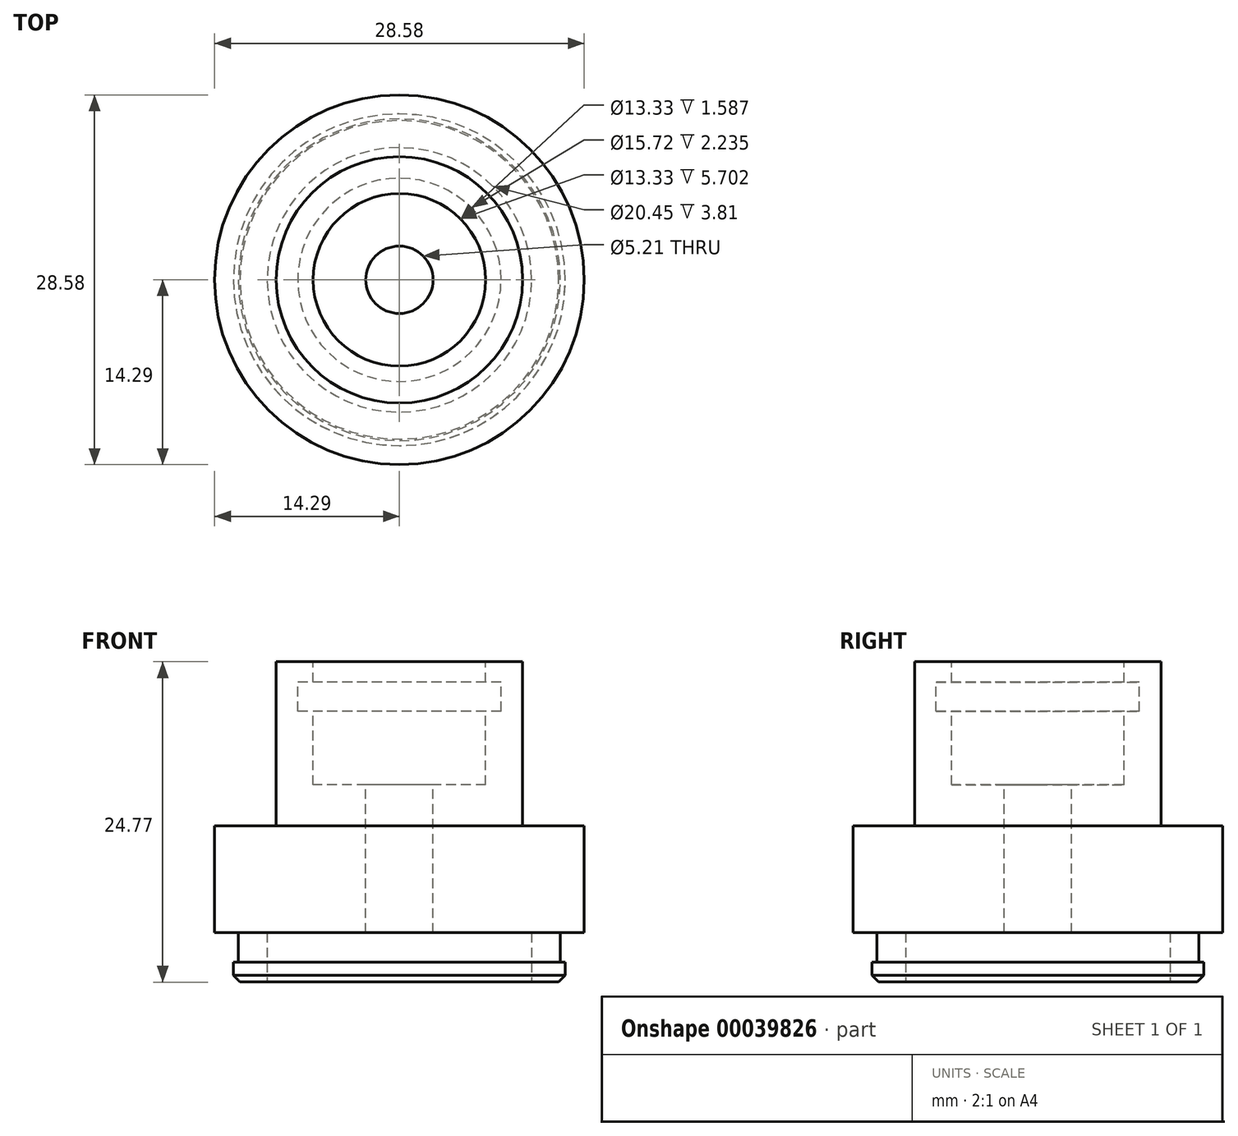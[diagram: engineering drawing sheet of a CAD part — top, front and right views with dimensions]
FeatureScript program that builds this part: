
annotation { "Feature Type Name" : "Feature", "Feature Type Description" : "" }
export const myFeature = defineFeature(function(context is Context, id is Id, definition is map)
    precondition{}
    {
        {
            var Q0;
            Q0=qCreatedBy(makeId("Top.planeOp"),FACE);
            var sketch = newSketch(context, id + "F0", { "sketchPlane" : qUnion([Q0])});
            skCircle(sketch, "E0", {"center": v(0, 0) * mm, "radius": 9.53 * mm});
            skSolve(sketch);
        }
        {
            var Q0;
            Q0=qSketchRegion(id+"F0",true);
            extrude(context, id + "F1", {"entities" : qUnion([Q0]), "depth" : 12.7 * mm});
        }
        {
            var Q0;
            Q0=makeQuery(id+"F1.opExtrude","CAP_FACE",FACE,{"disambiguationData":[OSD([sQuery(id+"F0.wireOp",EDGE,"E0")])],"isStart":false});
            var sketch = newSketch(context, id + "F2", { "sketchPlane" : qUnion([Q0])});
            skCircle(sketch, "E1", {"center": v(0, 0) * mm, "radius": 6.67 * mm});
            skSolve(sketch);
        }
        {
            var Q0;
            Q0=qSketchRegion(id+"F2",true);
            extrude(context, id + "F3", {"entities" : qUnion([Q0]), "operationType" : NewBodyOperationType.REMOVE, "oppositeDirection" : true, "depth" : 9.52 * mm});
        }
        {
            var Q0;
            Q0=qCreatedBy(makeId("Front.planeOp"),FACE);
            var sketch = newSketch(context, id + "F4", { "sketchPlane" : qUnion([Q0])});
            skLineSegment(sketch, "E2.bottom", {"start": v(6.67, 11.11) * mm, "end": v(7.86, 11.11) * mm});
            skLineSegment(sketch, "E2.top", {"start": v(6.67, 8.88) * mm, "end": v(7.86, 8.88) * mm});
            skLineSegment(sketch, "E2.left", {"start": v(6.67, 11.11) * mm, "end": v(6.67, 8.88) * mm});
            skLineSegment(sketch, "E2.right", {"start": v(7.86, 11.11) * mm, "end": v(7.86, 8.88) * mm});
            skLineSegment(sketch, "E3", {"start": v(0, 0) * mm, "end": v(0, 38.04) * mm, "construction": true});
            skSolve(sketch);
        }
        {
            var Q0;
            Q0=qSketchRegion(id+"F4",true);
            var Q1;
            Q1=sQuery(id+"F4.wireOp",EDGE,"E3");
            revolve(context, id + "F5", {"operationType" : NewBodyOperationType.REMOVE, "entities" : qUnion([Q0]), "axis" : qUnion([Q1]), "revolveType" : RevolveType.FULL, "oppositeDirection" : true});
        }
        {
            var Q0;
            Q0=makeQuery(id+"F1.opExtrude","CAP_FACE",FACE,{"disambiguationData":[OSD([sQuery(id+"F0.wireOp",EDGE,"E0")])],"isStart":true});
            var sketch = newSketch(context, id + "F6", { "sketchPlane" : qUnion([Q0])});
            skCircle(sketch, "E4", {"center": v(0, 0) * mm, "radius": 14.29 * mm});
            skSolve(sketch);
        }
        {
            var Q0;
            Q0=makeQuery(id+"F6.imprint","IMPRINT",FACE,{"disambiguationData":[TD([[makeQuery(id+"F6.imprint","IMPRINT",EDGE,{"derivedFrom":sQuery(id+"F6.wireOp",EDGE,"E4")}),1.0]])]});
            var Q1;
            Q1=makeQuery(id+"F6.imprint","IMPRINT",FACE,{"disambiguationData":[TD([[makeQuery(id+"F6.imprint","IMPRINT",EDGE,{"derivedFrom":makeQuery(id+"F15.boolean.opBoolean","INTERSECT",EDGE,{"derivedFrom":[makeQuery(id+"F1.opExtrude","CAP_FACE",FACE,{"disambiguationData":[OSD([sQuery(id+"F0.wireOp",EDGE,"E0")])],"isStart":true}),makeQuery(id+"F15.opExtrude","SWEPT_FACE",FACE,{"disambiguationData":[OSD([sQuery(id+"F14.wireOp",EDGE,"E9")])]})]})}),-1.0]])]});
            var Q2;
            {var subQ0=sQuery(id+"F0.wireOp",EDGE,"E0");Q2=makeQuery(id+"F6.imprint","IMPRINT",FACE,{"disambiguationData":[TD([[makeQuery(id+"F6.imprint","IMPRINT",EDGE,{"derivedFrom":makeQuery(id+"F1.opExtrude","CAP_EDGE",EDGE,{"disambiguationData":[OSD([subQ0])],"isStart":true})}),-1.0]])]});}
            extrude(context, id + "F7", {"entities" : qUnion([Q0, Q1, Q2]), "operationType" : NewBodyOperationType.ADD, "depth" : 8.25 * mm});
        }
        {
            var Q0;
            Q0=makeQuery(id+"F7.opExtrude","CAP_FACE",FACE,{"disambiguationData":[OSD([sQuery(id+"F6.wireOp",EDGE,"E4")])],"isStart":false});
            var sketch = newSketch(context, id + "F8", { "sketchPlane" : qUnion([Q0])});
            skCircle(sketch, "E5", {"center": v(0, 0) * mm, "radius": 12.83 * mm});
            skSolve(sketch);
        }
        {
            var Q0;
            Q0 = qSketchRegion(id + "F8", true);
            extrude(context, id + "F9", {"entities" : qUnion([Q0]), "operationType" : NewBodyOperationType.ADD, "depth" : 3.8 * mm});
        }
        {
            var Q0;
            Q0=makeQuery(id+"F9.opExtrude","CAP_FACE",FACE,{"disambiguationData":[OSD([sQuery(id+"F8.wireOp",EDGE,"E5")])],"isStart":false});
            var sketch = newSketch(context, id + "F10", { "sketchPlane" : qUnion([Q0])});
            skCircle(sketch, "E6", {"center": v(0, 0) * mm, "radius": 10.22 * mm});
            skSolve(sketch);
        }
        {
            var Q0;
            Q0 = qSketchRegion(id + "F10", true);
            extrude(context, id + "F11", {"entities" : qUnion([Q0]), "operationType" : NewBodyOperationType.REMOVE, "oppositeDirection" : true, "depth" : 3.8 * mm});
        }
        {
            var Q0;
            Q0=qCreatedBy(makeId("Front.planeOp"),FACE);
            var sketch = newSketch(context, id + "F12", { "sketchPlane" : qUnion([Q0])});
            skLineSegment(sketch, "E7.bottom", {"start": v(12.83, -10.54) * mm, "end": v(12.45, -10.54) * mm});
            skLineSegment(sketch, "E7.top", {"start": v(12.83, -8.26) * mm, "end": v(12.45, -8.26) * mm});
            skLineSegment(sketch, "E7.left", {"start": v(12.83, -10.54) * mm, "end": v(12.83, -8.26) * mm});
            skLineSegment(sketch, "E7.right", {"start": v(12.45, -10.54) * mm, "end": v(12.45, -8.26) * mm});
            skLineSegment(sketch, "E8", {"start": v(0, 0) * mm, "end": v(0, -17.86) * mm, "construction": true});
            skSolve(sketch);
        }
        {
            var Q0;
            Q0 = qSketchRegion(id + "F12", true);
            var Q1;
            Q1=sQuery(id+"F12.wireOp",EDGE,"E8");
            revolve(context, id + "F13", {"operationType" : NewBodyOperationType.REMOVE, "entities" : qUnion([Q0]), "axis" : qUnion([Q1]), "revolveType" : RevolveType.FULL});
        }
        {
            var Q0;
            Q0=makeQuery(id+"F3.boolean.opBoolean","COPY",FACE,{"derivedFrom":makeQuery(id+"F3.opExtrude","CAP_FACE",FACE,{"disambiguationData":[OSD([sQuery(id+"F2.wireOp",EDGE,"E1")])],"isStart":false})});
            var sketch = newSketch(context, id + "F14", { "sketchPlane" : qUnion([Q0])});
            skCircle(sketch, "E9", {"center": v(0, 0) * mm, "radius": 2.6 * mm});
            skSolve(sketch);
        }
        {
            var Q0;
            Q0=qSketchRegion(id+"F14",true);
            extrude(context, id + "F15", {"entities" : qUnion([Q0]), "operationType" : NewBodyOperationType.REMOVE, "oppositeDirection" : true, "depth" : 25.4 * mm, "hasSecondDirection" : true, "secondDirectionOppositeDirection" : false, "secondDirectionDepth" : 25.4 * mm});
        }
        {
            var Q0;
            Q0=makeQuery(id+"F11.boolean.opBoolean","COPY",EDGE,{"derivedFrom":makeQuery(id+"F11.opExtrude","CAP_EDGE",EDGE,{"disambiguationData":[OSD([sQuery(id+"F10.wireOp",EDGE,"E6")])],"isStart":true})});
            var Q1;
            Q1=makeQuery(id+"F9.opExtrude","CAP_EDGE",EDGE,{"disambiguationData":[OSD([sQuery(id+"F8.wireOp",EDGE,"E5")])],"isStart":false});
            chamfer(context, id + "F16", {"entities" : qUnion([Q0, Q1]), "width" : 0.5 * mm, "tangentPropagation" : true});
        }
    });
